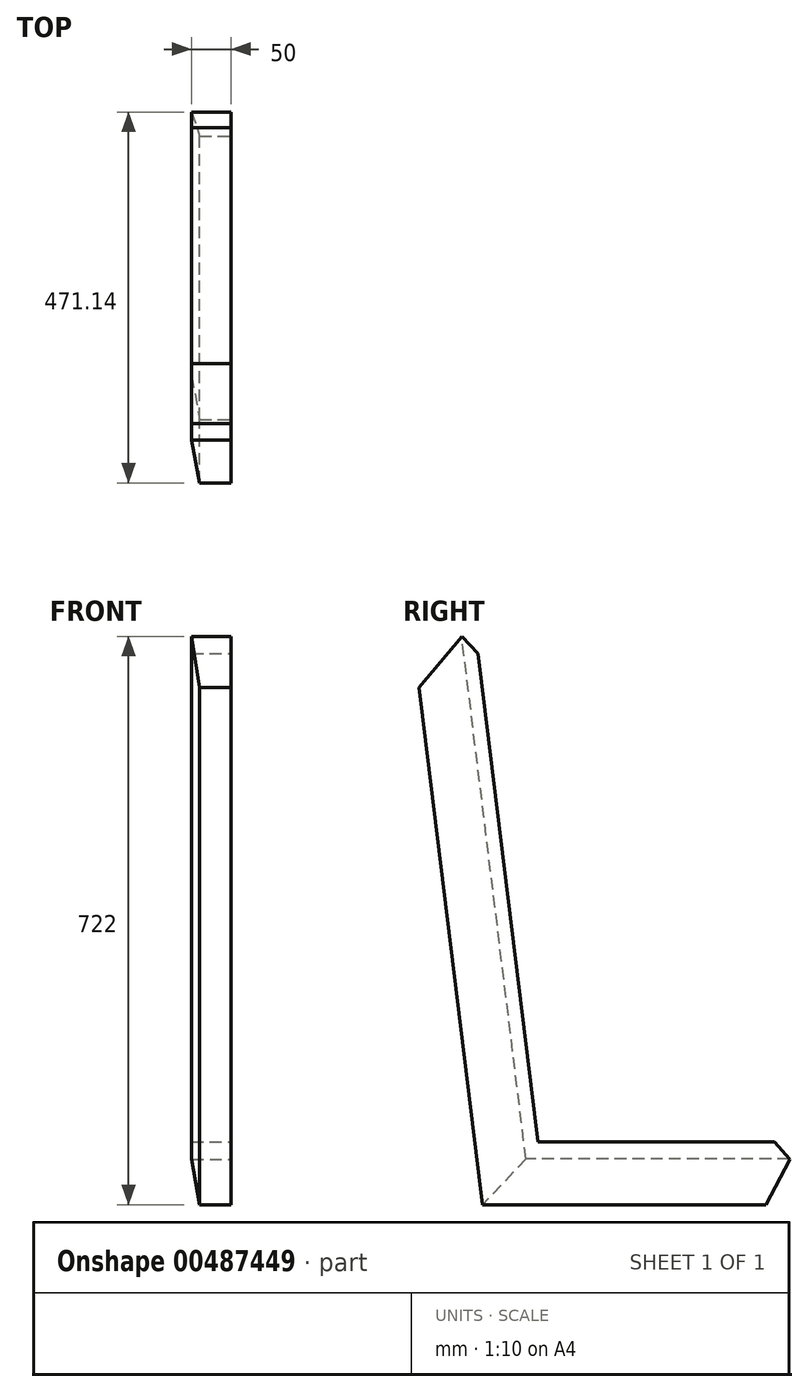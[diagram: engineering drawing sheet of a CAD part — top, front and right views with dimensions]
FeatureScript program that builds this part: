
annotation { "Feature Type Name" : "Feature", "Feature Type Description" : "" }
export const myFeature = defineFeature(function(context is Context, id is Id, definition is map)
    precondition{}
    {
        {
            var Q0;
            Q0=qCreatedBy(makeId("Right.planeOp"),FACE);
            var sketch = newSketch(context, id + "F0", { "sketchPlane" : qUnion([Q0])});
            skLineSegment(sketch, "E0.bottom", {"start": v(0, 0) * mm, "end": v(482.8, 0) * mm, "construction": true});
            skLineSegment(sketch, "E0.top", {"start": v(0, 1100) * mm, "end": v(482.8, 1100) * mm, "construction": true});
            skLineSegment(sketch, "E0.left", {"start": v(0, 0) * mm, "end": v(0, 1100) * mm, "construction": true});
            skLineSegment(sketch, "E0.right", {"start": v(482.8, 0) * mm, "end": v(482.8, 1100) * mm, "construction": true});
            skLineSegment(sketch, "E1", {"start": v(463.07, 400) * mm, "end": v(482.8, 377.4) * mm});
            skLineSegment(sketch, "E2", {"start": v(482.8, 377.4) * mm, "end": v(452.29, 320) * mm});
            skLineSegment(sketch, "E3", {"start": v(452.29, 320) * mm, "end": v(92.29, 320) * mm});
            skLineSegment(sketch, "E4", {"start": v(163.07, 400) * mm, "end": v(463.07, 400) * mm});
            skLineSegment(sketch, "E5", {"start": v(11.65, 976.76) * mm, "end": v(92.29, 320) * mm});
            skLineSegment(sketch, "E6", {"start": v(163.07, 400) * mm, "end": v(86.9, 1020.34) * mm});
            skLineSegment(sketch, "E7", {"start": v(86.9, 1020.34) * mm, "end": v(66.14, 1042) * mm});
            skLineSegment(sketch, "E8", {"start": v(66.14, 1042) * mm, "end": v(11.65, 976.76) * mm});
            skSolve(sketch);
        }
        {
            var Q0;
            Q0=qSketchRegion(id+"F0",true);
            extrude(context, id + "F1", {"entities" : qUnion([Q0]), "oppositeDirection" : true, "depth" : 50 * mm});
        }
        {
            var Q0;
            Q0=makeQuery(id+"F1.opExtrude","CAP_EDGE",EDGE,{"disambiguationData":[OSD([sQuery(id+"F0.wireOp",EDGE,"E3")])],"isStart":false});
            chamfer(context, id + "F2", {"entities" : qUnion([Q0]), "chamferType" : ChamferType.TWO_OFFSETS, "width1" : 58 * mm, "oppositeDirection" : false, "width2" : 10 * mm, "tangentPropagation" : true});
        }
        {
            var Q0;
            Q0=makeQuery(id+"F1.opExtrude","CAP_EDGE",EDGE,{"disambiguationData":[OSD([sQuery(id+"F0.wireOp",EDGE,"E5")])],"isStart":false});
            chamfer(context, id + "F3", {"entities" : qUnion([Q0]), "chamferType" : ChamferType.TWO_OFFSETS, "width1" : 10 * mm, "oppositeDirection" : false, "width2" : 62 * mm, "tangentPropagation" : true});
        }
    });
